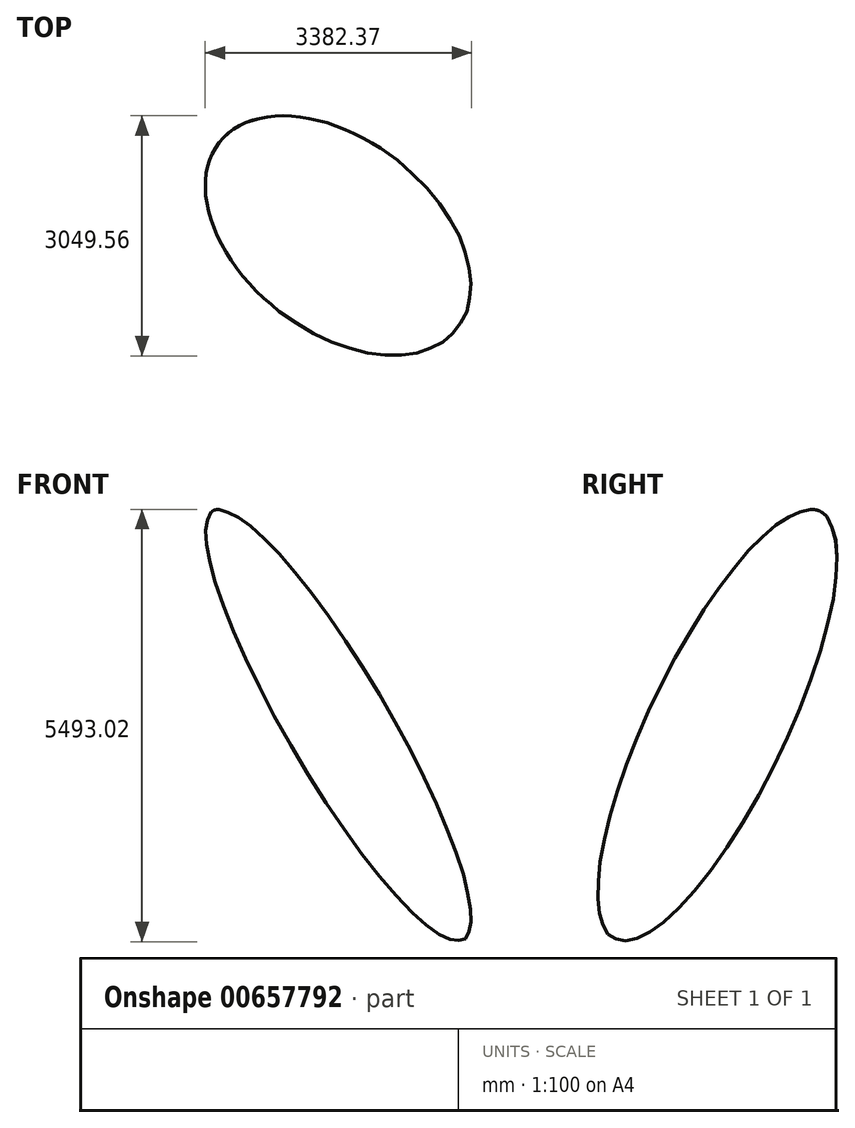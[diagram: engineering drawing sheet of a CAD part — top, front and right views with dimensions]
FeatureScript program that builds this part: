
annotation { "Feature Type Name" : "Feature", "Feature Type Description" : "" }
export const myFeature = defineFeature(function(context is Context, id is Id, definition is map)
    precondition{}
    {
        {
            assignVariable(context, id + "F0", {"name" : "Azimuth", "anyValue" : 38});
        }
        {
            assignVariable(context, id + "F1", {"name" : "Dip", "anyValue" : 55});
        }
        {
            assignVariable(context, id + "F2", {"name" : "Width", "anyValue" : .2});
        }
        {
            var Q0;
            Q0=qCreatedBy(makeId("Top.planeOp"),FACE);
            var sketch = newSketch(context, id + "F3", { "sketchPlane" : qUnion([Q0])});
            skEllipse(sketch, "E0", {"center": v(0, 0) * mm, "majorRadius": 1219.2 * mm, "minorRadius": 3352.8 * mm, "majorAxis": v(0, 1)});
            skLineSegment(sketch, "E1", {"start": v(0, 3550.92) * mm, "end": v(0, -3550.92) * mm, "construction": true});
            skLineSegment(sketch, "E2", {"start": v(-4328.16, 0) * mm, "end": v(4328.16, 0) * mm, "construction": true});
            skLineSegment(sketch, "E3.0", {"start": v(-731.52, 1219.2) * mm, "end": v(-731.52, -1219.2) * mm, "construction": true});
            skLineSegment(sketch, "E4.0", {"start": v(-3352.8, 1676.4) * mm, "end": v(3352.8, 1676.4) * mm, "construction": true});
            skSolve(sketch);
        }
        {
            var Q0;
            Q0=qCreatedBy(makeId("Top.planeOp"),FACE);
            var sketch = newSketch(context, id + "F4", { "sketchPlane" : qUnion([Q0])});
            skLineSegment(sketch, "E5", {"start": v(-731.52, 0) * mm, "end": v(0, 0) * mm});
            skLineSegment(sketch, "E6", {"start": v(-731.52, 1676.4) * mm, "end": v(-731.52, 0) * mm});
            skSolve(sketch);
        }
        {
            var Q0;
            Q0=qSketchRegion(id+"F3",true);
            extrude(context, id + "F5", {"entities" : qUnion([Q0]), "depth" : (getVariable(context, 'Width')) * mm});
        }
        {
            var Q0;
            Q0=qCreatedBy(makeId("Front.planeOp"),FACE);
            var sketch = newSketch(context, id + "F6", { "sketchPlane" : qUnion([Q0])});
            skLineSegment(sketch, "E7", {"start": v(0, 0) * mm, "end": v(0, -6096) * mm, "construction": true});
            skSolve(sketch);
        }
        {
            var Q0;
            Q0=makeQuery(id+"F5.opExtrude","SWEPT_BODY",BODY,{"disambiguationData":[OSD([sQuery(id+"F3.wireOp",EDGE,"E0"),sQuery(id+"F3.wireOp",EDGE,"TMMzbr5i-4nV4-ZnMr-aG6B-IGJ66UyS6uPJ")])]});
            var Q1;
            Q1=sQuery(id+"F3.wireOp",EDGE,"E1");
            transform(context, id + "F7", {"entities" : qUnion([Q0]), "transformType" : TransformType.ROTATION, "transformAxis" : qUnion([Q1]), "angle" : (getVariable(context, 'Dip')) * degree, "oppositeDirection" : true, "makeCopy" : false});
        }
        {
            var Q0;
            Q0=makeQuery(id+"F5.opExtrude","SWEPT_BODY",BODY,{"disambiguationData":[OSD([sQuery(id+"F3.wireOp",EDGE,"E0")])]});
            var Q1;
            Q1=sQuery(id+"F6.wireOp",EDGE,"E7");
            transform(context, id + "F8", {"entities" : qUnion([Q0]), "transformType" : TransformType.ROTATION, "transformAxis" : qUnion([Q1]), "angle" : (getVariable(context, 'Azimuth')) * degree, "makeCopy" : false});
        }
        {
            var Q0;
            Q0=makeQuery(id+"F5.opExtrude","SWEPT_BODY",BODY,{"disambiguationData":[OSD([sQuery(id+"F3.wireOp",EDGE,"E0"),sQuery(id+"F3.wireOp",EDGE,"TMMzbr5i-4nV4-ZnMr-aG6B-IGJ66UyS6uPJ")])]});
            var Q1;
            Q1=sQuery(id+"F4.wireOp",EDGE,"E5");
            transform(context, id + "F9", {"entities" : qUnion([Q0]), "transformType" : TransformType.TRANSLATION_ENTITY, "oppositeDirectionEntity" : true, "transformLine" : qUnion([Q1]), "makeCopy" : false});
        }
        {
            var Q0;
            Q0=makeQuery(id+"F5.opExtrude","SWEPT_BODY",BODY,{"disambiguationData":[OSD([sQuery(id+"F3.wireOp",EDGE,"E0"),sQuery(id+"F3.wireOp",EDGE,"TMMzbr5i-4nV4-ZnMr-aG6B-IGJ66UyS6uPJ")])]});
            var Q1;
            Q1=sQuery(id+"F4.wireOp",EDGE,"E6");
            transform(context, id + "F10", {"entities" : qUnion([Q0]), "transformType" : TransformType.TRANSLATION_ENTITY, "oppositeDirectionEntity" : true, "transformLine" : qUnion([Q1]), "makeCopy" : false});
        }
        {
            var Q0;
            Q0=qCreatedBy(makeId("Top.planeOp"),FACE);
            var sketch = newSketch(context, id + "F11", { "sketchPlane" : qUnion([Q0])});
            skCircle(sketch, "E8", {"center": v(0, 0) * mm, "radius": 76.2 * mm});
            skSolve(sketch);
        }
        {
            var Q0;
            Q0=qSketchRegion(id+"F11",true);
            extrude(context, id + "F12", {"entities" : qUnion([Q0]), "operationType" : NewBodyOperationType.REMOVE, "endBound" : BoundingType.THROUGH_ALL, "oppositeDirection" : true, "depth" : 30.48 * mm, "hasSecondDirection" : true, "secondDirectionBound" : SecondDirectionBoundingType.THROUGH_ALL, "secondDirectionOppositeDirection" : false, "secondDirectionDepth" : 30.48 * mm});
        }
        {
            var Q0;
            Q0=makeQuery(id+"F5.opExtrude","SWEPT_BODY",BODY,{"disambiguationData":[OSD([sQuery(id+"F3.wireOp",EDGE,"E0")])]});
            var Q1;
            Q1=sQuery(id+"F6.wireOp",EDGE,"E7");
            transform(context, id + "F13", {"entities" : qUnion([Q0]), "transformType" : TransformType.TRANSLATION_3D, "dx" : 0 * mm, "dy" : 0 * mm, "dz" : -3810 * mm, "makeCopy" : false});
        }
    });
